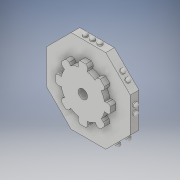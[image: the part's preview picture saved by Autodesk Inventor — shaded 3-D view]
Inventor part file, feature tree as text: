
AUTODESK INVENTOR PART (.ipt)
format: ipt  version: 2017 (Build 210142000, 142)  size: 351,744 bytes
history: native  units: in
note: dims shown in document units (in); Inventor stores cm internally (conversion verified against a paired STEP export)
features: sketch x11, extrude x10, fillet x7, pattern_circular x1
ambient origin geometry x8: Origin, YZ Plane, XZ Plane, XY Plane, X Axis, Y Axis, Z Axis, Center Point
bodies: Solid1 (feature_tree)
feature tree (29):
  extrude  "Extrusion1"  Depth=0.1181in TaperAngle=0.0deg
  extrude  "Extrusion2"  Depth=0.063in
  fillet  "Fillet1"  Radius=0.1in
  sketch  "Sketch3"  dims[d8=0.063in d9=0.063in d10=0.059in]
  sketch  "Sketch4"  dims[d11=0.0472in d12=0.0in d13=0.0315in d24=0.059in]
  sketch  "Sketch5"  dims[d25=0.063in d26=0.1in d27=0.1in d28=0.063in d29=0.063in d31=0.0575in d32=0.059in d34=0.0in d35=0.059in]
  sketch  "Sketch6"  dims[d36=0.059in]
  sketch  "Sketch7"  dims[d40=0.063in d41=0.1in d42=0.1in d43=0.063in d44=0.063in d46=0.059in d47=0.0in d48=0.059in d49=0.059in d50=0.0in d51=0.0in]
  sketch  "Sketch8"  dims[d70=0.063in d71=0.1in d72=0.1in d73=0.063in d74=0.063in d76=0.059in d77=0.0in d78=0.059in d79=0.059in d81=0.0in d82=0.0in]
  sketch  "Sketch9"  dims[d83=0.063in d84=0.1in d85=0.1in d86=0.063in d87=0.063in d89=0.059in d90=0.059in d91=0.059in d92=0.0in d93=0.0in d94=0.0in d95=0.0in]
  extrude  "Extrusion6"  Depth=0.063in
  fillet  "Fillet5"  Radius=0.059in
  extrude  "Extrusion7"  Depth=0.0315in
  fillet  "Fillet6"  Radius=0.059in
  extrude  "Extrusion8"  TaperAngle=0.0deg  [1 undecoded]
  fillet  "Fillet7"  Radius=0.059in
  extrude  "Extrusion9"  TaperAngle=0.0deg  [1 undecoded]
  fillet  "Fillet8"  [1 undecoded]
  extrude  "Extrusion10"  TaperAngle=0.0deg  [1 undecoded]
  fillet  "Fillet9"  [1 undecoded]
  extrude  "Extrusion11"  TaperAngle=0.0deg  [1 undecoded]
  fillet  "Fillet10"  [1 undecoded]
  extrude  "Extrusion14"  Depth=0.0315in
  pattern_circular  "Circular Pattern4"  [2 undecoded]
  extrude  "Extrusion15"  Depth=0.0315in
  sketch  "Sketch1"  dims[d2=0.4724in d3=0.1181in d4=0.0in]
  sketch  "Sketch2"  dims[d5=0.063in d6=0.1in d7=0.1in]
  sketch  "Sketch11"  dims[d96=0.063in d97=0.1in d98=0.1in d99=0.063in d100=0.063in d102=0.059in d103=0.059in d104=0.059in d105=0.0in d106=0.0in d107=0.0in d108=0.0in]
  sketch  "Sketch12"  dims[d109=0.063in d110=0.1in d111=0.1in d112=0.063in d113=0.063in d115=0.059in d116=0.059in d117=0.059in d118=0.0in d119=0.0in d120=0.0in d121=0.0in d122=0.0472in d123=0.0in d124=0.0315in d125=0.0472in d126=0.0in d127=0.0315in d128=0.0472in d129=0.0in d130=0.0315in d131=0.0472in d132=0.0in d133=0.0315in d134=0.0472in d135=0.0in d136=0.0315in d137=0.0472in d138=0.0in d139=0.0315in d148=0.6in d154=12.5984in d156=360.0deg d161=0.04in d162=0.04in d163=0.075in d164=0.0in d165=3.1496in d166=360.0deg d168=0.075in d169=0.236in d170=0.236in d171=0.236in d172=0.236in d173=0.236in d175=0.236in d176=0.236in d177=0.126in d178=1.0in d179=0.0in]
note: 9 required parameter values undecoded (feature->parameter linkage not recoverable at this tier; creation-order binding heuristic only, values carry confidence <= 0.55)
